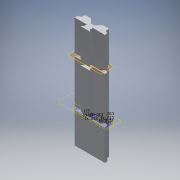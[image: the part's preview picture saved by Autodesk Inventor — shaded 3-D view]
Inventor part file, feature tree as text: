
AUTODESK INVENTOR PART (.ipt)
format: ipt  version: 2019 (Build 230136000, 136)  size: 247,808 bytes
history: native  units: in
note: dims shown in document units (in); Inventor stores cm internally (conversion verified against a paired STEP export)
features: extrude x5, sketch x4, projected_geometry x3, other x3, mirror x2, plane x2, reference x1
ambient origin geometry x8: Origin, YZ Plane, XZ Plane, XY Plane, X Axis, Y Axis, Z Axis, Center Point
bodies: Solid1 (feature_tree)
feature tree (20):
  sketch  "Sketch1"  dims[d1=0.0125in d2=0.0125in]
  extrude  "Extrusion1"  Depth=0.0125in
  extrude  "Extrusion2"  Depth=0.0125in
  mirror  "Mirror1"
  extrude  "Extrusion3"  Depth=3.0in TaperAngle=0.0deg
  plane  "Work Plane1"
  extrude  "Extrusion4"  Depth=0.125in
  plane  "Work Plane2"
  extrude  "Extrusion5"  Depth=0.125in
  mirror  "Mirror2"
  reference  "Reference1"
  sketch  "Sketch2"  dims[d3=0.0125in d4=0.0125in]
  projected_geometry  "Projected Loop1"
  sketch  "Sketch3"  dims[d5=0.0125in d7=3.0in d8=0.0in]
  projected_geometry  "Projected Loop2"
  projected_geometry  "Projected Loop3"
  parser-record x1  (decoder bookkeeping rows leaked as tree rows — omitted from the tree; the rows remain in map.json)
  other  "Pen_Holder_Assem.iam"
  other  "Holder_Mount:1"
  sketch  "Sketch4"  dims[d9=1.5in d10=0.0in d12=0.125in d13=0.0125in d14=30.0deg d15=0.4in d16=0.185in d17=45.0deg d18=0.125in d19=1.0in d20=0.0in d21=-1.25in d22=0.04in d23=0.04in d24=0.04in d25=0.04in d26=45.0deg d27=0.05in d28=0.125in d29=0.0in d30=-1.25in d37=0.04in d38=45.0deg d39=0.04in d40=0.05in d41=0.125in d42=0.0in]
note: 1 file-system path scrubbed to <path> (originals preserved in map.json)
